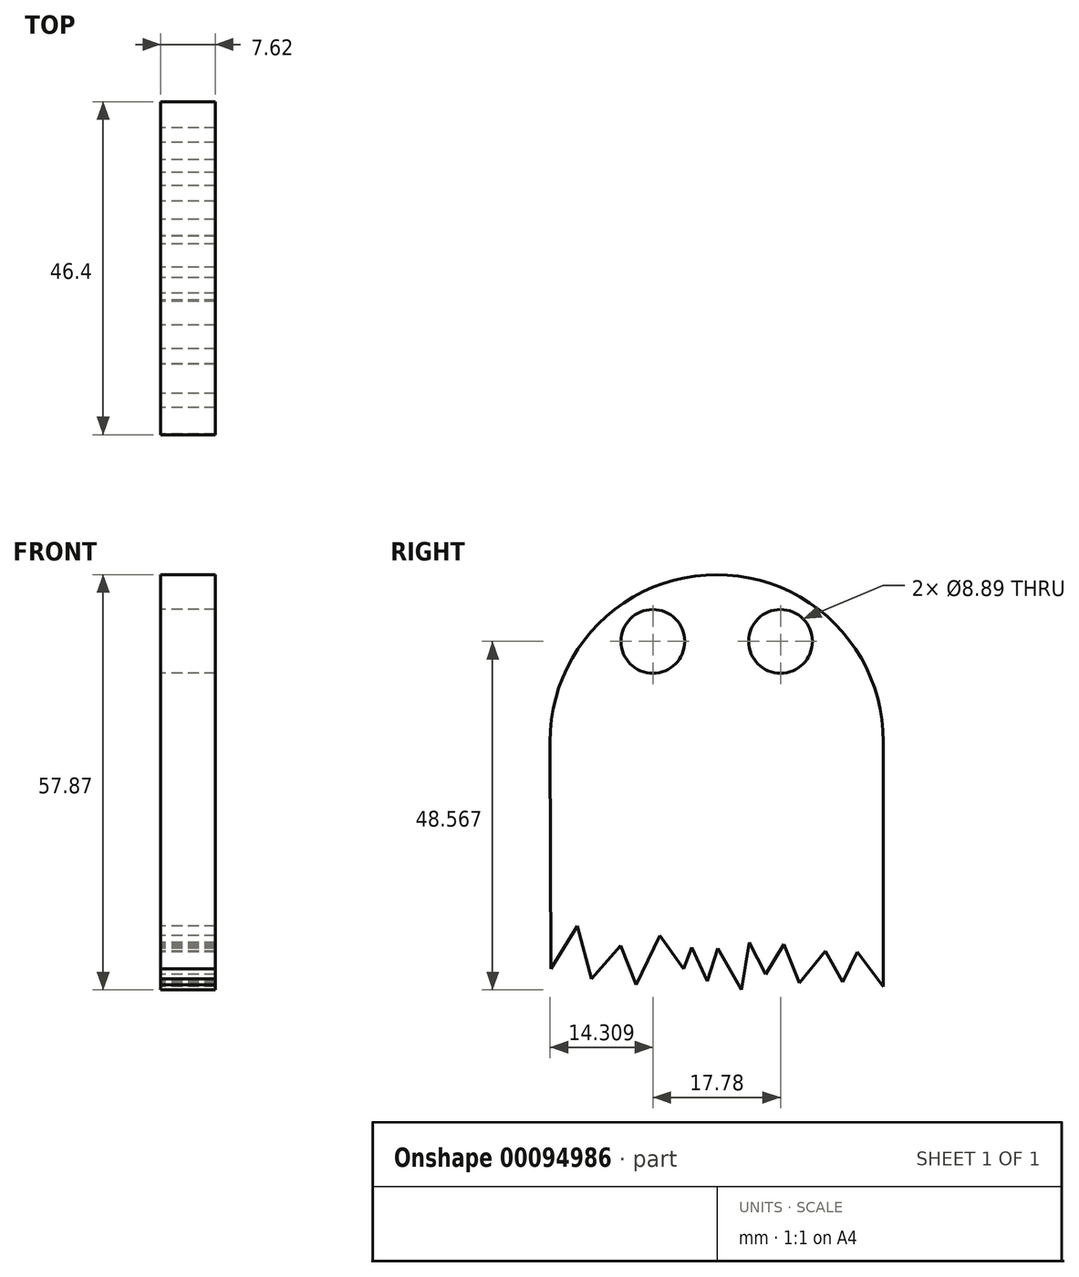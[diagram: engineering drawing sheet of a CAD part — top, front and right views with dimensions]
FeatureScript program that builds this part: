
annotation { "Feature Type Name" : "Feature", "Feature Type Description" : "" }
export const myFeature = defineFeature(function(context is Context, id is Id, definition is map)
    precondition{}
    {
        {
            var Q0;
            Q0=qCreatedBy(makeId("Right.planeOp"),FACE);
            var sketch = newSketch(context, id + "F0", { "sketchPlane" : qUnion([Q0])});
            skLineSegment(sketch, "E0", {"start": v(-36.58, 20.47) * mm, "end": v(9.82, 20.47) * mm, "construction": true});
            skArc(sketch, "E1", {"start": v(9.82, 20.47) * mm, "mid": v(-13.38, 43.78) * mm, "end": v(-36.58, 20.47) * mm});
            skLineSegment(sketch, "E2", {"start": v(-36.58, 20.47) * mm, "end": v(-36.44, -11.18) * mm});
            skLineSegment(sketch, "E3", {"start": v(-36.44, -11.18) * mm, "end": v(-32.76, -5.18) * mm});
            skLineSegment(sketch, "E4", {"start": v(-32.76, -5.18) * mm, "end": v(-30.85, -12.55) * mm});
            skLineSegment(sketch, "E5", {"start": v(-30.85, -12.55) * mm, "end": v(-26.76, -7.91) * mm});
            skLineSegment(sketch, "E6", {"start": v(-26.76, -7.91) * mm, "end": v(-24.57, -13.37) * mm});
            skLineSegment(sketch, "E7", {"start": v(-24.57, -13.37) * mm, "end": v(-21.3, -6.55) * mm});
            skLineSegment(sketch, "E8", {"start": v(-21.3, -6.55) * mm, "end": v(-18.02, -11.19) * mm});
            skLineSegment(sketch, "E9", {"start": v(-18.02, -11.19) * mm, "end": v(-16.83, -8.19) * mm});
            skLineSegment(sketch, "E10", {"start": v(-16.83, -8.19) * mm, "end": v(-14.66, -12.89) * mm});
            skLineSegment(sketch, "E11", {"start": v(-14.66, -12.89) * mm, "end": v(-13.22, -8.3) * mm});
            skLineSegment(sketch, "E12", {"start": v(-13.22, -8.3) * mm, "end": v(-9.96, -14.1) * mm});
            skLineSegment(sketch, "E13", {"start": v(-9.96, -14.1) * mm, "end": v(-8.87, -7.46) * mm});
            skLineSegment(sketch, "E14", {"start": v(-8.87, -7.46) * mm, "end": v(-6.58, -11.92) * mm});
            skLineSegment(sketch, "E15", {"start": v(-6.58, -11.92) * mm, "end": v(-4.05, -7.7) * mm});
            skLineSegment(sketch, "E16", {"start": v(-4.05, -7.7) * mm, "end": v(-1.88, -13.13) * mm});
            skLineSegment(sketch, "E17", {"start": v(-1.88, -13.13) * mm, "end": v(1.74, -8.67) * mm});
            skLineSegment(sketch, "E18", {"start": v(1.74, -8.67) * mm, "end": v(4.15, -13) * mm});
            skLineSegment(sketch, "E19", {"start": v(4.15, -13) * mm, "end": v(6.2, -8.79) * mm});
            skLineSegment(sketch, "E20", {"start": v(9.82, 20.47) * mm, "end": v(9.82, -13.65) * mm});
            skLineSegment(sketch, "E21", {"start": v(9.82, -13.65) * mm, "end": v(6.2, -8.79) * mm});
            skLineSegment(sketch, "E22", {"start": v(-13.38, 43.78) * mm, "end": v(-13.38, -29.25) * mm, "construction": true});
            skLineSegment(sketch, "E23", {"start": v(-13.38, 34.48) * mm, "end": v(-4.5, 34.48) * mm, "construction": true});
            skLineSegment(sketch, "E24", {"start": v(-13.38, 34.48) * mm, "end": v(-22.27, 34.48) * mm, "construction": true});
            skCircle(sketch, "E25", {"center": v(-22.27, 34.48) * mm, "radius": 4.45 * mm});
            skCircle(sketch, "E26", {"center": v(-4.5, 34.48) * mm, "radius": 4.45 * mm});
            skLineSegment(sketch, "E27", {"start": v(-22.27, 34.48) * mm, "end": v(-22.27, 38.92) * mm, "construction": true});
            skLineSegment(sketch, "E28", {"start": v(-22.27, 34.48) * mm, "end": v(-22.27, 30.03) * mm, "construction": true});
            skLineSegment(sketch, "E29", {"start": v(-4.5, 34.48) * mm, "end": v(-4.5, 38.92) * mm, "construction": true});
            skLineSegment(sketch, "E30", {"start": v(-4.5, 34.48) * mm, "end": v(-4.5, 30.03) * mm, "construction": true});
            skArc(sketch, "E31", {"start": v(-22.27, 30.03) * mm, "mid": v(-20.46, 34.48) * mm, "end": v(-22.27, 38.92) * mm});
            skArc(sketch, "E32", {"start": v(-22.27, 38.92) * mm, "mid": v(-24.09, 34.48) * mm, "end": v(-22.27, 30.03) * mm});
            skArc(sketch, "E33", {"start": v(-4.5, 30.03) * mm, "mid": v(-2.68, 34.48) * mm, "end": v(-4.5, 38.92) * mm});
            skArc(sketch, "E34", {"start": v(-4.5, 38.92) * mm, "mid": v(-6.3, 34.48) * mm, "end": v(-4.5, 30.03) * mm});
            skLineSegment(sketch, "E35", {"start": v(-20.46, 34.48) * mm, "end": v(-24.09, 34.48) * mm, "construction": true});
            skLineSegment(sketch, "E36", {"start": v(-6.3, 34.48) * mm, "end": v(-2.68, 34.48) * mm, "construction": true});
            skArc(sketch, "E37", {"start": v(-20.46, 34.48) * mm, "mid": v(-22.27, 36.3) * mm, "end": v(-24.09, 34.48) * mm});
            skArc(sketch, "E38", {"start": v(-24.09, 34.48) * mm, "mid": v(-22.27, 32.68) * mm, "end": v(-20.46, 34.48) * mm});
            skArc(sketch, "E39", {"start": v(-2.68, 34.48) * mm, "mid": v(-4.5, 36.31) * mm, "end": v(-6.3, 34.48) * mm});
            skArc(sketch, "E40", {"start": v(-6.3, 34.48) * mm, "mid": v(-4.5, 32.67) * mm, "end": v(-2.68, 34.48) * mm});
            skSolve(sketch);
        }
        {
            var Q0;
            Q0=makeQuery(id+"F0.imprint","IMPRINT",FACE,{"disambiguationData":[TD([[makeQuery(id+"F0.imprint","IMPRINT",EDGE,{"derivedFrom":sQuery(id+"F0.wireOp",EDGE,"E1")}),1.0]])]});
            extrude(context, id + "F1", {"entities" : qUnion([Q0]), "depth" : 7.62 * mm});
        }
    });
